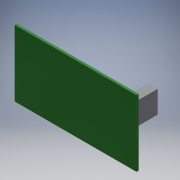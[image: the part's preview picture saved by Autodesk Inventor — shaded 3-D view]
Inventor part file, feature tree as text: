
AUTODESK INVENTOR PART (.ipt)
format: ipt  version: 2018 (Build 220112000, 112)  size: 190,464 bytes
history: native  units: mm
features: extrude x5, sketch x5
ambient origin geometry x8: Origin, YZ Plane, XZ Plane, XY Plane, X Axis, Y Axis, Z Axis, Center Point
bodies: Solid1 (feature_tree)
feature tree (10):
  extrude  "Extrusion1"  Depth=86.95mm
  extrude  "Extrusion4"  Depth=48.0mm
  extrude  "Extrusion5"  Depth=15.3mm
  extrude  "Extrusion6"  Depth=4.1mm
  extrude  "Extrusion7"  Depth=15.3mm
  sketch  "Sketch1"  dims[d0=160.0mm d1=86.95mm]
  sketch  "Sketch2"  dims[d2=3.0mm d3=0.0mm d6=48.0mm]
  sketch  "Sketch4"  dims[d7=20.4mm d26=15.3mm]
  sketch  "Sketch5"  dims[d27=22.1mm d29=4.1mm]
  sketch  "Sketch6"  dims[d30=15.3mm d32=15.3mm d36=12.4mm d37=29.3mm d38=15.3mm d42=15.3mm d44=15.3mm d46=6.1mm d47=6.1mm d48=6.1mm d49=6.1mm d50=6.1mm d51=11.4mm d52=10.4mm d53=17.0mm d54=73.4mm d55=11.7mm d56=10.0mm d57=0.0mm d58=3.0mm d59=0.0mm d60=15.2mm d61=5.6mm d62=27.45mm d63=14.2mm d64=15.2mm d65=5.6mm d66=4.1mm d67=8.5mm d68=0.0mm d69=25.0mm d70=0.0mm]
